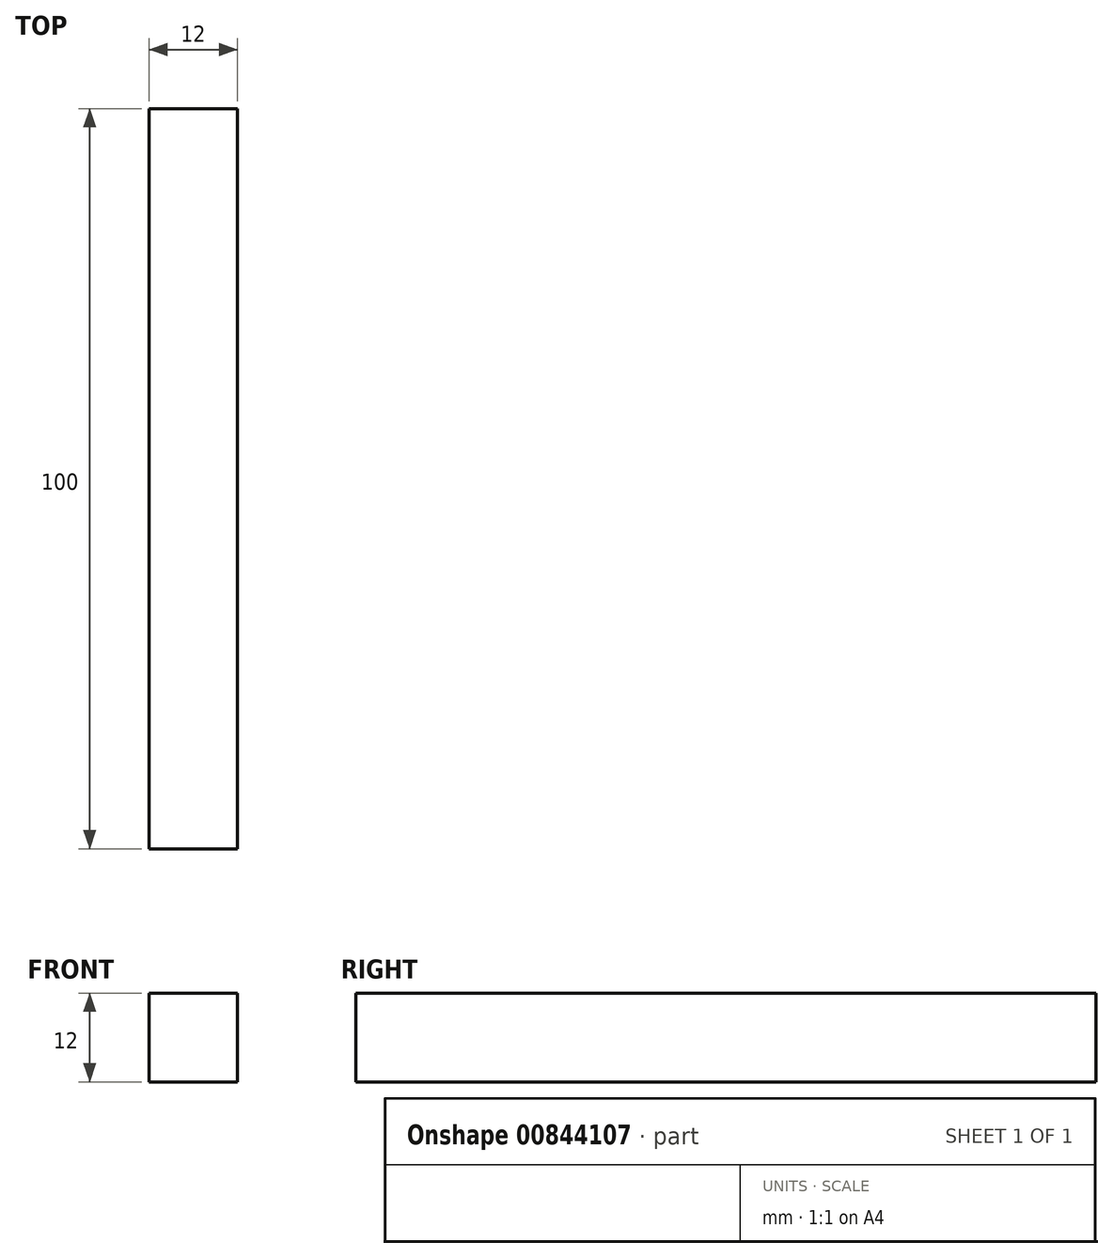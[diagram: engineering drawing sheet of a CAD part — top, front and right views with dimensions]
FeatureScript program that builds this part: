
annotation { "Feature Type Name" : "Feature", "Feature Type Description" : "" }
export const myFeature = defineFeature(function(context is Context, id is Id, definition is map)
    precondition{}
    {
        {
            var Q0;
            Q0=qCreatedBy(makeId("Front.planeOp"),FACE);
            var sketch = newSketch(context, id + "F0", { "sketchPlane" : qUnion([Q0])});
            skLineSegment(sketch, "E0.bottom", {"start": v(-6, 6) * mm, "end": v(6, 6) * mm});
            skLineSegment(sketch, "E0.top", {"start": v(-6, -6) * mm, "end": v(6, -6) * mm});
            skLineSegment(sketch, "E0.left", {"start": v(-6, 6) * mm, "end": v(-6, -6) * mm});
            skLineSegment(sketch, "E0.right", {"start": v(6, 6) * mm, "end": v(6, -6) * mm});
            skSolve(sketch);
        }
        {
            var Q0;
            Q0=makeQuery(id+"F0.imprint","IMPRINT",FACE,{"disambiguationData":[TD([[makeQuery(id+"F0.imprint","IMPRINT",EDGE,{"derivedFrom":sQuery(id+"F0.wireOp",EDGE,"E0.bottom")}),-1.0]])]});
            extrude(context, id + "F1", {"entities" : qUnion([Q0]), "endBound" : BoundingType.SYMMETRIC, "depth" : 100 * mm, "offsetDistance" : 25.4 * mm});
        }
    });
